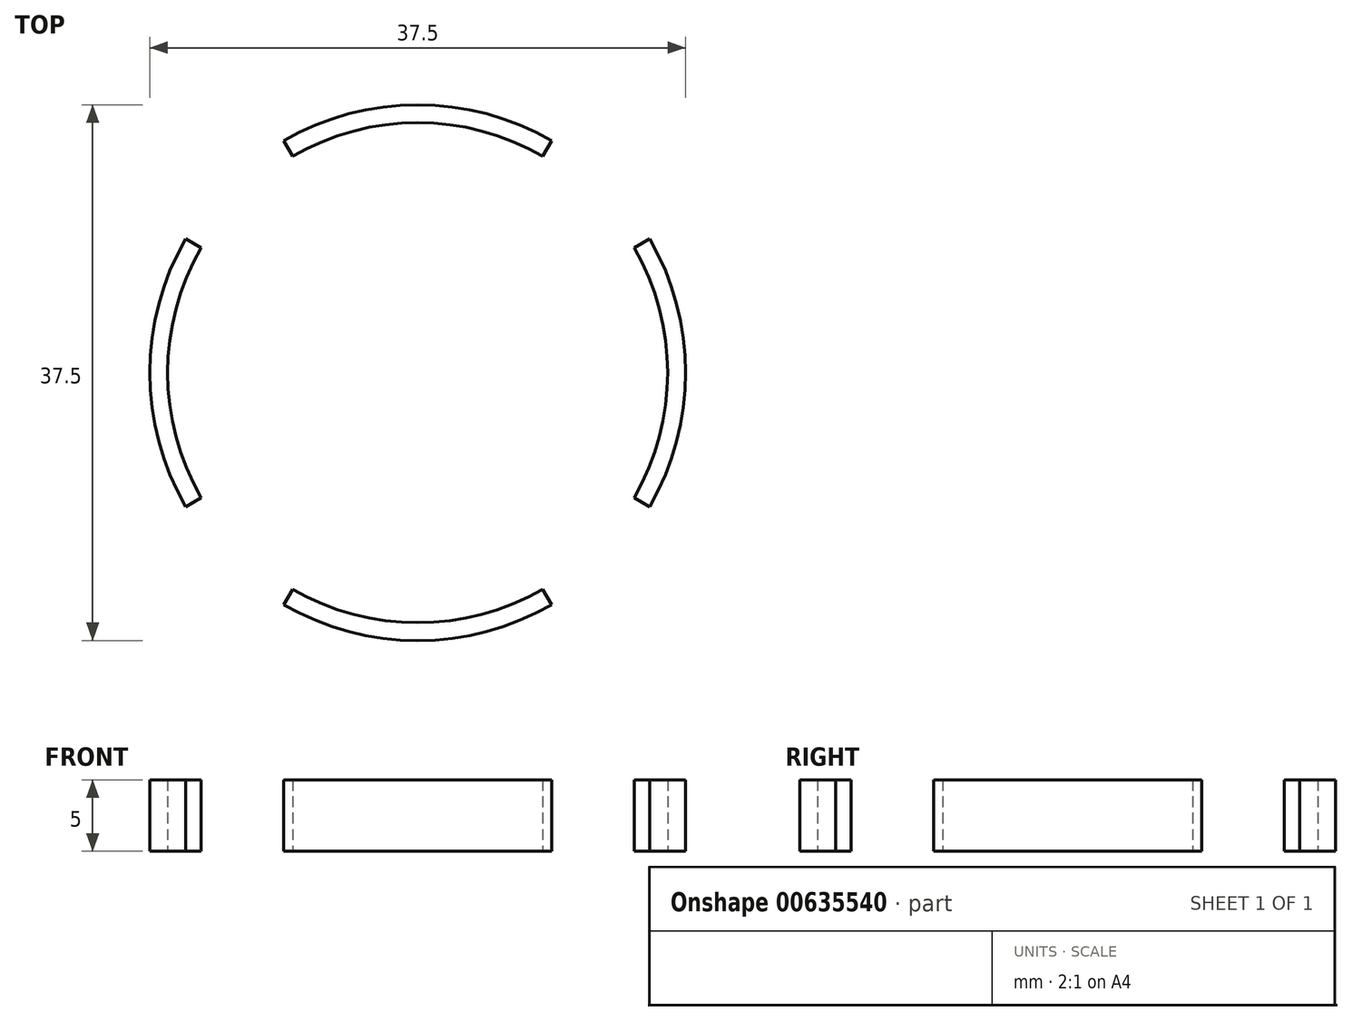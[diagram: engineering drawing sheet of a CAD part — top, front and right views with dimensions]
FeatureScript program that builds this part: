
annotation { "Feature Type Name" : "Feature", "Feature Type Description" : "" }
export const myFeature = defineFeature(function(context is Context, id is Id, definition is map)
    precondition{}
    {
        {
            var Q0;
            Q0=qCreatedBy(makeId("Top.planeOp"),FACE);
            var sketch = newSketch(context, id + "F0", { "sketchPlane" : qUnion([Q0])});
            skCircle(sketch, "E0", {"center": v(0, 0) * mm, "radius": 17.5 * mm, "construction": true});
            skCircle(sketch, "E1", {"center": v(0, 0) * mm, "radius": 18.75 * mm, "construction": true});
            skLineSegment(sketch, "E2", {"start": v(0, 0) * mm, "end": v(-16.24, 9.38) * mm, "construction": true});
            skLineSegment(sketch, "E3.MirrorCS", {"start": v(0, 0) * mm, "end": v(-16.24, -9.38) * mm, "construction": true});
            skLineSegment(sketch, "E4", {"start": v(0, 0) * mm, "end": v(-9.38, 16.24) * mm, "construction": true});
            skLineSegment(sketch, "E5.MirrorCS", {"start": v(0, 0) * mm, "end": v(9.37, 16.24) * mm, "construction": true});
            skLineSegment(sketch, "E6", {"start": v(0, 0) * mm, "end": v(16.24, 9.38) * mm, "construction": true});
            skLineSegment(sketch, "E7.MirrorCS", {"start": v(0, 0) * mm, "end": v(16.24, -9.38) * mm, "construction": true});
            skLineSegment(sketch, "E8", {"start": v(0, 0) * mm, "end": v(9.38, -16.24) * mm, "construction": true});
            skLineSegment(sketch, "E9.MirrorCS", {"start": v(0, 0) * mm, "end": v(-9.38, -16.24) * mm, "construction": true});
            skLineSegment(sketch, "E10", {"start": v(-8.75, 15.16) * mm, "end": v(-9.38, 16.24) * mm});
            skLineSegment(sketch, "E11", {"start": v(-15.16, 8.75) * mm, "end": v(-16.24, 9.38) * mm});
            skLineSegment(sketch, "E12", {"start": v(-15.16, -8.75) * mm, "end": v(-16.24, -9.38) * mm});
            skLineSegment(sketch, "E13", {"start": v(-8.75, -15.16) * mm, "end": v(-9.38, -16.24) * mm});
            skLineSegment(sketch, "E14", {"start": v(8.75, -15.16) * mm, "end": v(9.38, -16.24) * mm});
            skLineSegment(sketch, "E15", {"start": v(15.16, -8.75) * mm, "end": v(16.24, -9.38) * mm});
            skLineSegment(sketch, "E16", {"start": v(15.16, 8.75) * mm, "end": v(16.24, 9.38) * mm});
            skLineSegment(sketch, "E17", {"start": v(8.75, 15.16) * mm, "end": v(9.37, 16.24) * mm});
            skLineSegment(sketch, "E18", {"start": v(0, 0) * mm, "end": v(-13.26, -13.26) * mm, "construction": true});
            skLineSegment(sketch, "E19", {"start": v(0, 0) * mm, "end": v(13.26, -13.26) * mm, "construction": true});
            skLineSegment(sketch, "E20.MirrorCS", {"start": v(0, 0) * mm, "end": v(13.26, 13.26) * mm, "construction": true});
            skLineSegment(sketch, "E21.MirrorCS", {"start": v(0, 0) * mm, "end": v(-13.26, 13.26) * mm, "construction": true});
            skArc(sketch, "E22", {"start": v(-15.16, -8.75) * mm, "mid": v(-17.5, 0) * mm, "end": v(-15.16, 8.75) * mm});
            skArc(sketch, "E23", {"start": v(-16.24, -9.37) * mm, "mid": v(-18.75, 0) * mm, "end": v(-16.24, 9.38) * mm});
            skArc(sketch, "E24", {"start": v(-8.75, 15.16) * mm, "mid": v(0, 17.5) * mm, "end": v(8.75, 15.16) * mm});
            skArc(sketch, "E25", {"start": v(-9.38, 16.24) * mm, "mid": v(0, 18.75) * mm, "end": v(9.37, 16.24) * mm});
            skArc(sketch, "E26", {"start": v(15.16, 8.75) * mm, "mid": v(17.5, 0) * mm, "end": v(15.16, -8.75) * mm});
            skArc(sketch, "E27", {"start": v(16.24, 9.38) * mm, "mid": v(18.75, 0) * mm, "end": v(16.24, -9.37) * mm});
            skArc(sketch, "E28", {"start": v(-8.75, -15.16) * mm, "mid": v(-13.32, 11.35) * mm, "end": v(13.58, 11.04) * mm});
            skArc(sketch, "E29", {"start": v(8.75, -15.16) * mm, "mid": v(0, -17.5) * mm, "end": v(-8.75, -15.16) * mm});
            skArc(sketch, "E30", {"start": v(9.38, -16.24) * mm, "mid": v(0, -18.75) * mm, "end": v(-9.38, -16.24) * mm});
            skSolve(sketch);
        }
        {
            var Q0;
            {var subQ0=sQuery(id+"F0.wireOp",EDGE,"E11");Q0=makeQuery(id+"F0.imprint","IMPRINT",FACE,{"disambiguationData":[TD([[makeQuery(id+"F0.imprint","IMPRINT",EDGE,{"derivedFrom":subQ0}),1.0]])]});}
            var Q1;
            Q1=makeQuery(id+"F0.imprint","IMPRINT",FACE,{"disambiguationData":[TD([[makeQuery(id+"F0.imprint","IMPRINT",EDGE,{"derivedFrom":sQuery(id+"F0.wireOp",EDGE,"E13")}),1.0]])]});
            var Q2;
            Q2=makeQuery(id+"F0.imprint","IMPRINT",FACE,{"disambiguationData":[TD([[makeQuery(id+"F0.imprint","IMPRINT",EDGE,{"derivedFrom":sQuery(id+"F0.wireOp",EDGE,"E15")}),1.0]])]});
            var Q3;
            {var subQ0=sQuery(id+"F0.wireOp",EDGE,"E10");Q3=makeQuery(id+"F0.imprint","IMPRINT",FACE,{"disambiguationData":[TD([[makeQuery(id+"F0.imprint","IMPRINT",EDGE,{"derivedFrom":subQ0}),-1.0]])]});}
            extrude(context, id + "F1", {"entities" : qUnion([Q0, Q1, Q2, Q3]), "depth" : 5 * mm, "offsetDistance" : 25 * mm});
        }
    });
